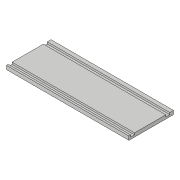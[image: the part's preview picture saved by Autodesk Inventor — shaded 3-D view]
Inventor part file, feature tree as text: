
AUTODESK INVENTOR PART (.ipt)
format: ipt  version: 2018.3 (Build 223284000, 284)  size: 97,792 bytes
history: native  units: in
note: dims shown in document units (in); Inventor stores cm internally (conversion verified against a paired STEP export)
features: extrude x2, sketch x2
ambient origin geometry x8: Origin, YZ Plane, XZ Plane, XY Plane, X Axis, Y Axis, Z Axis, Center Point
bodies: Solid1 (feature_tree)
feature tree (4):
  extrude  "Extrusion1"  Depth=1.5in
  extrude  "Extrusion2"  Depth=0.126in
  sketch  "Sketch1"  dims[d0=4.125in d1=1.5in]
  sketch  "Sketch2"  dims[d2=0.125in d3=0.0in d4=0.126in d6=0.0625in d7=0.0in d8=0.0625in d13=0.125in d14=0.135in]
